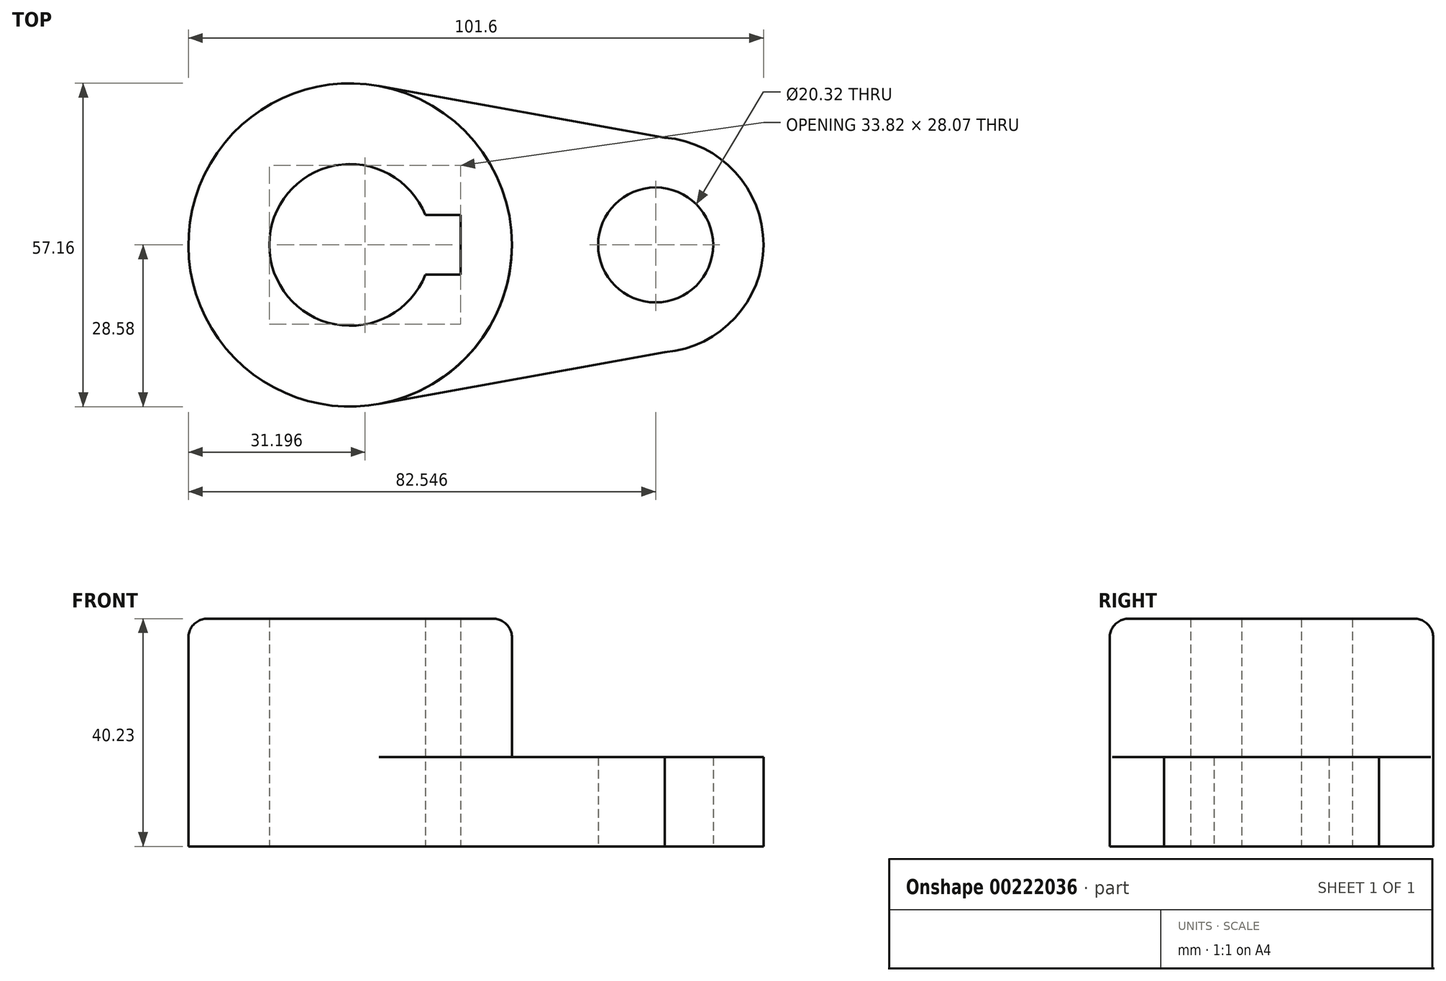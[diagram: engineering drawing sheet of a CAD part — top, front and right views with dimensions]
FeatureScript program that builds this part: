
annotation { "Feature Type Name" : "Feature", "Feature Type Description" : "" }
export const myFeature = defineFeature(function(context is Context, id is Id, definition is map)
    precondition{}
    {
        {
            var Q0;
            Q0=qCreatedBy(makeId("Top.planeOp"),FACE);
            var sketch = newSketch(context, id + "F0", { "sketchPlane" : qUnion([Q0])});
            skArc(sketch, "E0", {"start": v(-30.44, 5.27) * mm, "mid": v(-58, 0) * mm, "end": v(-30.44, -5.27) * mm});
            skCircle(sketch, "E1", {"center": v(-43.72, 0) * mm, "radius": 28.58 * mm});
            skCircle(sketch, "E2", {"center": v(10.26, 0) * mm, "radius": 10.16 * mm});
            skArc(sketch, "E3", {"start": v(11.9, -18.98) * mm, "mid": v(29.3, 0) * mm, "end": v(11.9, 18.98) * mm});
            skLineSegment(sketch, "E4.bottom", {"start": v(-24.18, -5.27) * mm, "end": v(-30.44, -5.27) * mm});
            skLineSegment(sketch, "E4.top", {"start": v(-24.18, 5.27) * mm, "end": v(-30.44, 5.27) * mm});
            skLineSegment(sketch, "E4.left", {"start": v(-24.18, -5.27) * mm, "end": v(-24.18, 5.27) * mm});
            skPoint(sketch, "E5.start.orphan", {"position": v(-57, 5.27) * mm});
            skPoint(sketch, "E6.orphan", {"position": v(-63.26, 5.27) * mm});
            skPoint(sketch, "E7.orphan", {"position": v(-63.26, -5.27) * mm});
            skLineSegment(sketch, "E8", {"start": v(11.9, 18.98) * mm, "end": v(-38.63, 28.12) * mm});
            skLineSegment(sketch, "E9", {"start": v(-38.63, -28.12) * mm, "end": v(11.9, -18.98) * mm});
            skSolve(sketch);
        }
        {
            var Q0;
            Q0=makeQuery(id+"F0.imprint","IMPRINT",FACE,{"disambiguationData":[TD([[makeQuery(id+"F0.imprint","IMPRINT",EDGE,{"derivedFrom":sQuery(id+"F0.wireOp",EDGE,"E0")}),-1.0]])]});
            extrude(context, id + "F1", {"entities" : qUnion([Q0]), "depth" : 40.23 * mm});
        }
        {
            var Q0;
            Q0 = qSketchRegion(id + "F0", true);
            extrude(context, id + "F2", {"entities" : qUnion([Q0]), "operationType" : NewBodyOperationType.ADD, "depth" : 15.77 * mm});
        }
        {
            var Q0;
            Q0=makeQuery(id+"F1.opExtrude","CAP_EDGE",EDGE,{"disambiguationData":[OSD([sQuery(id+"F0.wireOp",EDGE,"E1")])],"isStart":false});
            fillet(context, id + "F3", {"entities" : qUnion([Q0]), "radius" : 3.3 * mm, "tangentPropagation" : true, "allowEdgeOverflow" : false});
        }
    });
